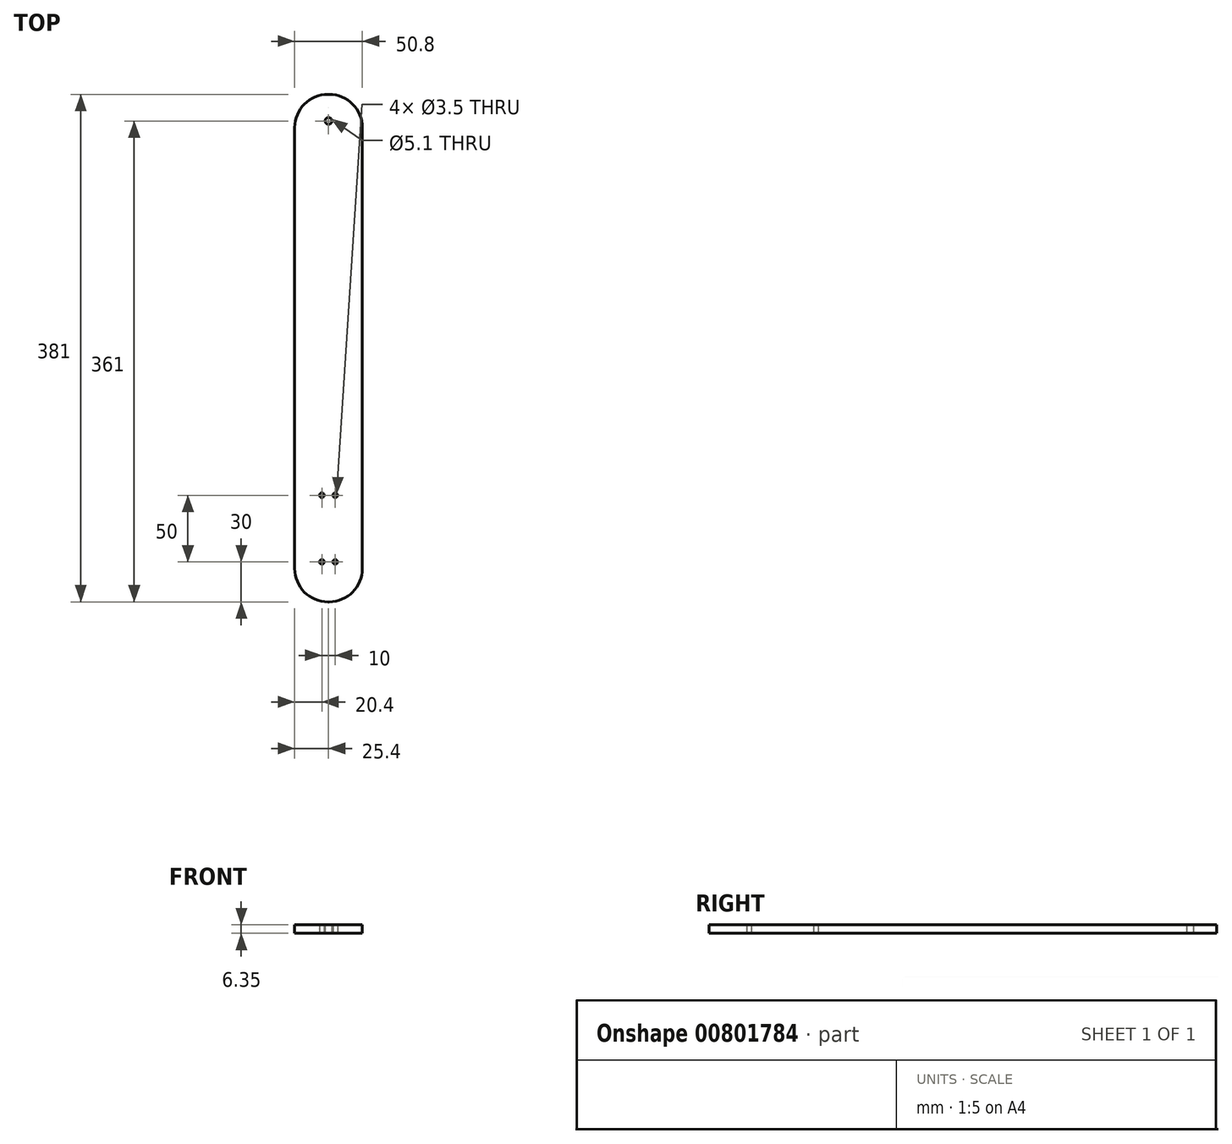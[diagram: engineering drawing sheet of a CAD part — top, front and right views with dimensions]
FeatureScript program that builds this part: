
annotation { "Feature Type Name" : "Feature", "Feature Type Description" : "" }
export const myFeature = defineFeature(function(context is Context, id is Id, definition is map)
    precondition{}
    {
        {
            var Q0;
            Q0=qCreatedBy(makeId("Top.planeOp"),FACE);
            var sketch = newSketch(context, id + "F0", { "sketchPlane" : qUnion([Q0])});
            skLineSegment(sketch, "E0.bottom", {"start": v(0.4, 190.5) * mm, "end": v(-0.4, 190.5) * mm});
            skLineSegment(sketch, "E0.top", {"start": v(0.4, -190.5) * mm, "end": v(-0.4, -190.5) * mm});
            skLineSegment(sketch, "E0.left", {"start": v(25.4, 165.5) * mm, "end": v(25.4, -165.5) * mm});
            skLineSegment(sketch, "E0.right", {"start": v(-25.4, 165.5) * mm, "end": v(-25.4, -165.5) * mm});
            skPoint(sketch, "E0.middle", {"position": v(0, 0) * mm});
            skCircle(sketch, "E1", {"center": v(0, 170.5) * mm, "radius": 2.55 * mm});
            skPoint(sketch, "E2.visualSharp", {"position": v(-25.4, -190.5) * mm});
            skArc(sketch, "E2.filletArc", {"start": v(-25.4, -165.5) * mm, "mid": v(-18.08, -183.18) * mm, "end": v(-0.4, -190.5) * mm});
            skPoint(sketch, "E3.visualSharp", {"position": v(25.4, -190.5) * mm});
            skArc(sketch, "E3.filletArc", {"start": v(0.4, -190.5) * mm, "mid": v(18.08, -183.18) * mm, "end": v(25.4, -165.5) * mm});
            skPoint(sketch, "E4.visualSharp", {"position": v(25.4, 190.5) * mm});
            skArc(sketch, "E4.filletArc", {"start": v(25.4, 165.5) * mm, "mid": v(18.08, 183.18) * mm, "end": v(0.4, 190.5) * mm});
            skPoint(sketch, "E5.visualSharp", {"position": v(-25.4, 190.5) * mm});
            skArc(sketch, "E5.filletArc", {"start": v(-0.4, 190.5) * mm, "mid": v(-18.08, 183.18) * mm, "end": v(-25.4, 165.5) * mm});
            skCircle(sketch, "E6.MirrorC", {"center": v(5, -110.5) * mm, "radius": 1.75 * mm});
            skCircle(sketch, "E7.MirrorC", {"center": v(-5, -110.5) * mm, "radius": 1.75 * mm});
            skCircle(sketch, "E8.MirrorC", {"center": v(-5, -160.5) * mm, "radius": 1.75 * mm});
            skCircle(sketch, "E9.MirrorC", {"center": v(5, -160.5) * mm, "radius": 1.75 * mm});
            skLineSegment(sketch, "E10", {"start": v(-5, -110.5) * mm, "end": v(5, -110.5) * mm, "construction": true});
            skLineSegment(sketch, "E11", {"start": v(-5, -160.5) * mm, "end": v(5, -160.5) * mm, "construction": true});
            skSolve(sketch);
        }
        {
            var Q0;
            Q0=makeQuery(id+"F0.imprint","IMPRINT",FACE,{"disambiguationData":[TD([[makeQuery(id+"F0.imprint","IMPRINT",EDGE,{"derivedFrom":sQuery(id+"F0.wireOp",EDGE,"E0.bottom")}),1.0]])]});
            extrude(context, id + "F1", {"entities" : qUnion([Q0]), "depth" : 6.35 * mm, "offsetDistance" : 25 * mm});
        }
    });
